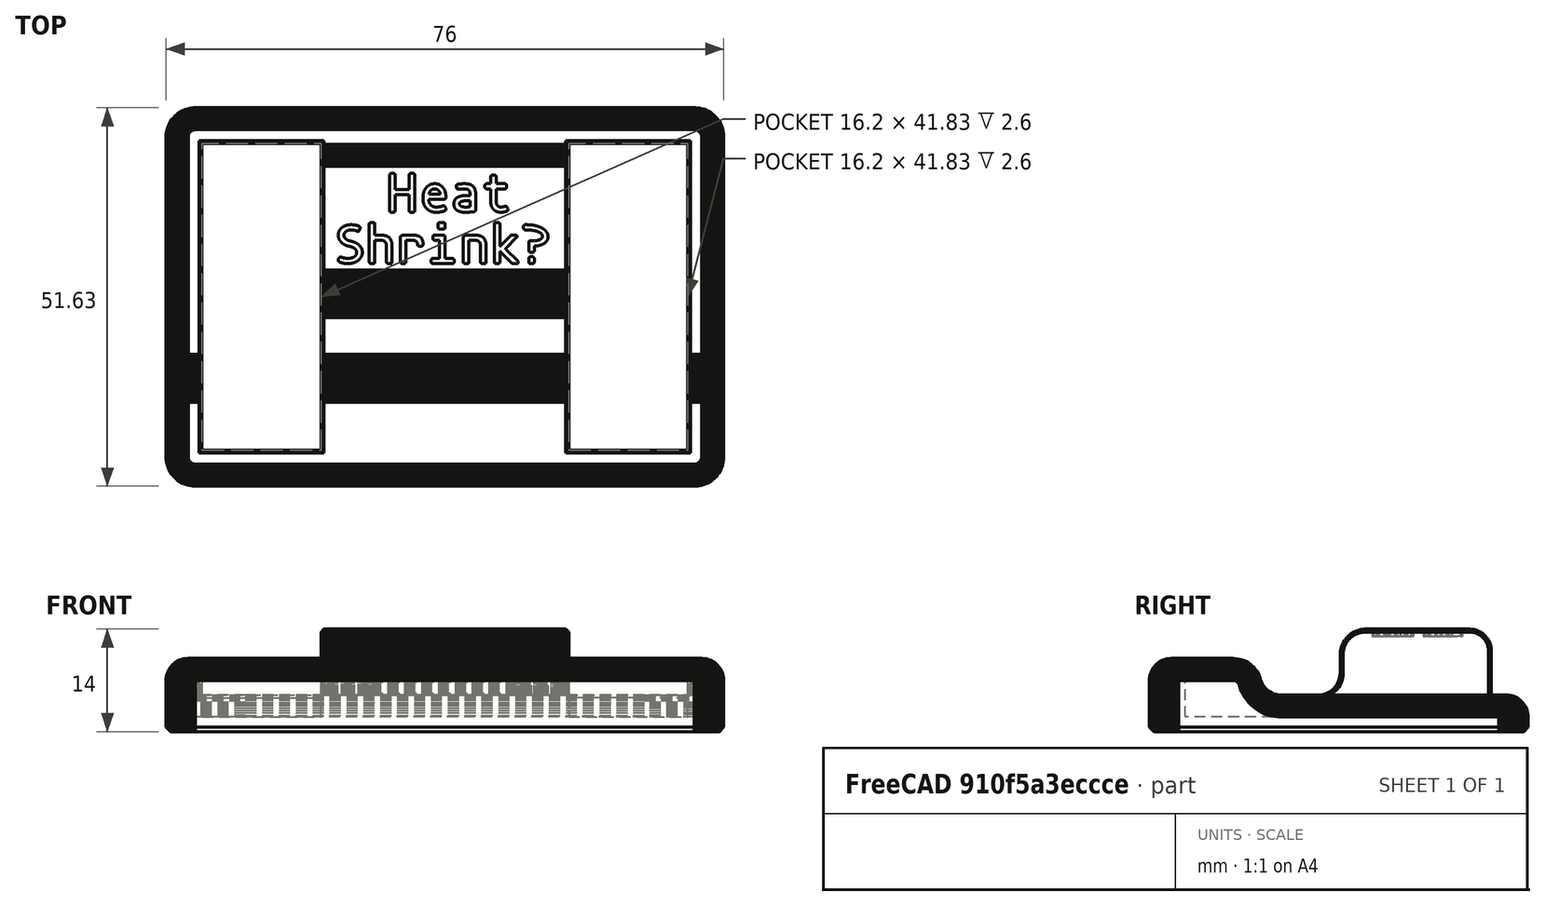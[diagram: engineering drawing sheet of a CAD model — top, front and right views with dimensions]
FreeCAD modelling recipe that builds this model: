
FCSTD DOCUMENT  (FreeCAD 0.19R14555 (Git shallow))
Label: wire_fingers
License: All rights reserved
LicenseURL: http://en.wikipedia.org/wiki/All_rights_reserved
objects: Part::Part2DObjectPython×2, Part::Extrusion×2, Part::Cut×2, Part::Feature×1, Mesh::Feature×1
note: 7 computed .brp shape members not serialized (recipe doc carries the construction recipe); baked Part::Feature solids carry a one-line shape summary decoded from their .brp

FEATURE [Part::Feature] Common_solid  label="Common (Solid)"
  shape: bbox 76 x 51.63 x 14 mm, 5532 faces (baked)
FEATURE [Part::Part2DObjectPython] ShapeString  # Draft 2D object (typed FeaturePython)
  AttachmentOffset = pos=(31,38,0) rot=(0,0,1;0rad)
  FontFile = /run/user/1000/doc/65262425/mononoki-Bold.ttf
  MapMode = 5
  Placement = pos=(31,38,15.0075) rot=(0,0,1;0rad)
  Size = 3
  String = Heat
  Support = -> [Common_solid]
  Tracking = 0
FEATURE [Part::Part2DObjectPython] ShapeString001  # Draft 2D object (typed FeaturePython)
  AttachmentOffset = pos=(24,31,0) rot=(0,0,1;0rad)
  FontFile = /run/user/1000/doc/65262425/mononoki-Bold.ttf
  MapMode = 5
  Placement = pos=(24,31,15.0075) rot=(0,0,1;0rad)
  Size = 3
  String = Shrink?
  Support = -> [Common_solid]
  Tracking = 0
FEATURE [Part::Extrusion] Extrude
  Base = -> ShapeString
  Dir = (0,0,1)
  DirMode = 2
  FaceMakerClass = Part::FaceMakerBullseye
  LengthFwd = 1
  LengthRev = 0
  Reversed = true
  Solid = false
  Symmetric = false
FEATURE [Part::Extrusion] Extrude001
  Base = -> ShapeString001
  Dir = (0,0,1)
  DirMode = 2
  FaceMakerClass = Part::FaceMakerBullseye
  LengthFwd = 1
  LengthRev = 0
  Reversed = true
  Solid = false
  Symmetric = false
FEATURE [Part::Cut] Cut
  Base = -> Common_solid
  Tool = -> Extrude
FEATURE [Part::Cut] Cut001
  Base = -> Cut
  Tool = -> Extrude001
FEATURE [Mesh::Feature] Mesh  label="Cut001 (Meshed)"
